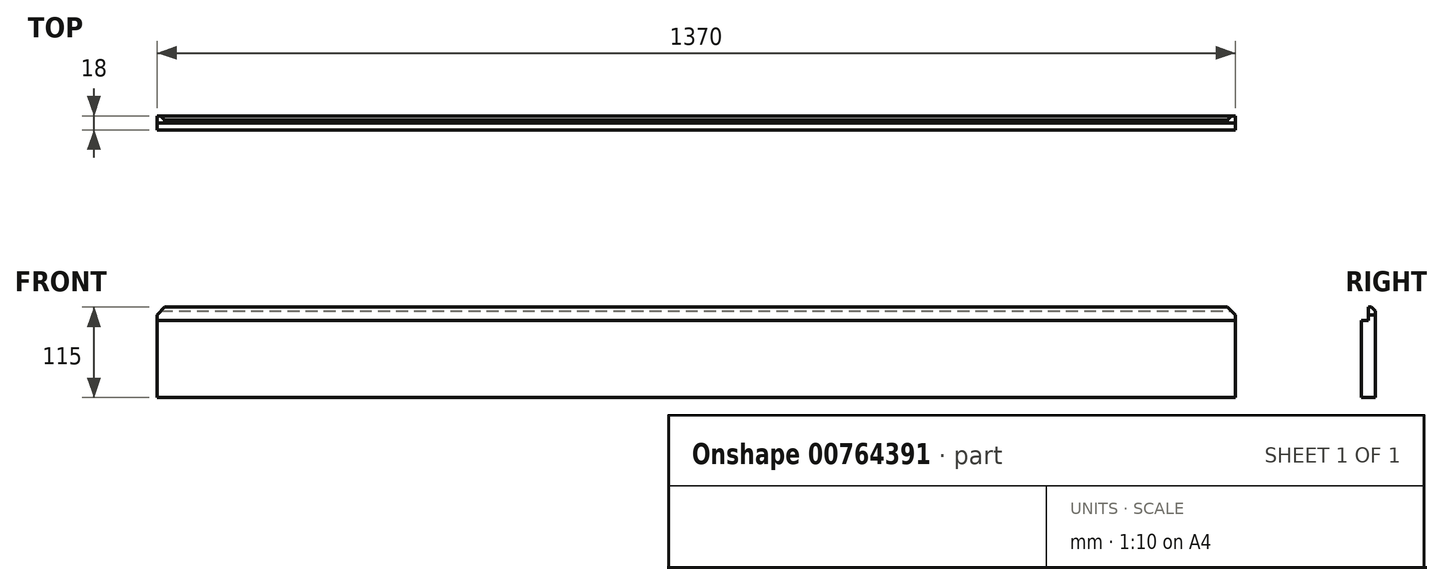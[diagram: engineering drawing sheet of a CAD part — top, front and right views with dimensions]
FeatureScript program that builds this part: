
annotation { "Feature Type Name" : "Feature", "Feature Type Description" : "" }
export const myFeature = defineFeature(function(context is Context, id is Id, definition is map)
    precondition{}
    {
        {
            var Q0;
            Q0=qCreatedBy(makeId("Front.planeOp"),FACE);
            var sketch = newSketch(context, id + "F0", { "sketchPlane" : qUnion([Q0])});
            skLineSegment(sketch, "E0.bottom", {"start": v(685, 57.5) * mm, "end": v(-685, 57.5) * mm});
            skLineSegment(sketch, "E0.top", {"start": v(685, -57.5) * mm, "end": v(-685, -57.5) * mm});
            skLineSegment(sketch, "E0.left", {"start": v(685, 57.5) * mm, "end": v(685, -57.5) * mm});
            skLineSegment(sketch, "E0.right", {"start": v(-685, 57.5) * mm, "end": v(-685, -57.5) * mm});
            skPoint(sketch, "E0.middle", {"position": v(0, 0) * mm});
            skSolve(sketch);
        }
        {
            var Q0;
            Q0=makeQuery(id+"F0.imprint","IMPRINT",FACE,{"disambiguationData":[TD([[makeQuery(id+"F0.imprint","IMPRINT",EDGE,{"derivedFrom":sQuery(id+"F0.wireOp",EDGE,"E0.bottom")}),1.0]])]});
            extrude(context, id + "F1", {"entities" : qUnion([Q0]), "depth" : 9 * mm, "offsetDistance" : 25 * mm});
        }
        {
            var Q0;
            Q0=makeQuery(id+"F1.opExtrude","CAP_FACE",FACE,{"disambiguationData":[OSD([sQuery(id+"F0.wireOp",EDGE,"E0.bottom"),sQuery(id+"F0.wireOp",EDGE,"E0.top"),sQuery(id+"F0.wireOp",EDGE,"E0.left"),sQuery(id+"F0.wireOp",EDGE,"E0.right")])],"isStart":false});
            var sketch = newSketch(context, id + "F2", { "sketchPlane" : qUnion([Q0])});
            skLineSegment(sketch, "E1.bottom", {"start": v(-685, -57.5) * mm, "end": v(685, -57.5) * mm});
            skLineSegment(sketch, "E1.top", {"start": v(-685, 40.5) * mm, "end": v(685, 40.5) * mm});
            skLineSegment(sketch, "E1.left", {"start": v(-685, -57.5) * mm, "end": v(-685, 40.5) * mm});
            skLineSegment(sketch, "E1.right", {"start": v(685, -57.5) * mm, "end": v(685, 40.5) * mm});
            skSolve(sketch);
        }
        {
            var Q0;
            Q0=makeQuery(id+"F2.imprint","IMPRINT",FACE,{"disambiguationData":[TD([[makeQuery(id+"F2.imprint","IMPRINT",EDGE,{"derivedFrom":sQuery(id+"F2.wireOp",EDGE,"E1.bottom")}),-1.0]])]});
            extrude(context, id + "F3", {"entities" : qUnion([Q0]), "operationType" : NewBodyOperationType.ADD, "depth" : 9 * mm, "offsetDistance" : 25 * mm});
        }
        {
            var Q0;
            Q0=makeQuery(id+"F1.opExtrude","CAP_EDGE",EDGE,{"disambiguationData":[OSD([sQuery(id+"F0.wireOp",EDGE,"E0.bottom")])],"isStart":true});
            chamfer(context, id + "F4", {"entities" : qUnion([Q0]), "width" : 5 * mm, "tangentPropagation" : true});
        }
        {
            var Q0;
            Q0=makeQuery(id+"F1.opExtrude","SWEPT_EDGE",EDGE,{"disambiguationData":[OSD([sQuery(id+"F0.wireOp",EDGE,"E0.bottom"),sQuery(id+"F0.wireOp",EDGE,"E0.left")])]});
            chamfer(context, id + "F5", {"entities" : qUnion([Q0]), "width" : 10 * mm, "tangentPropagation" : true});
        }
        {
            var Q0;
            Q0=makeQuery(id+"F1.opExtrude","SWEPT_EDGE",EDGE,{"disambiguationData":[OSD([sQuery(id+"F0.wireOp",EDGE,"E0.bottom"),sQuery(id+"F0.wireOp",EDGE,"E0.right")])]});
            chamfer(context, id + "F6", {"entities" : qUnion([Q0]), "width" : 10 * mm, "tangentPropagation" : true});
        }
    });
